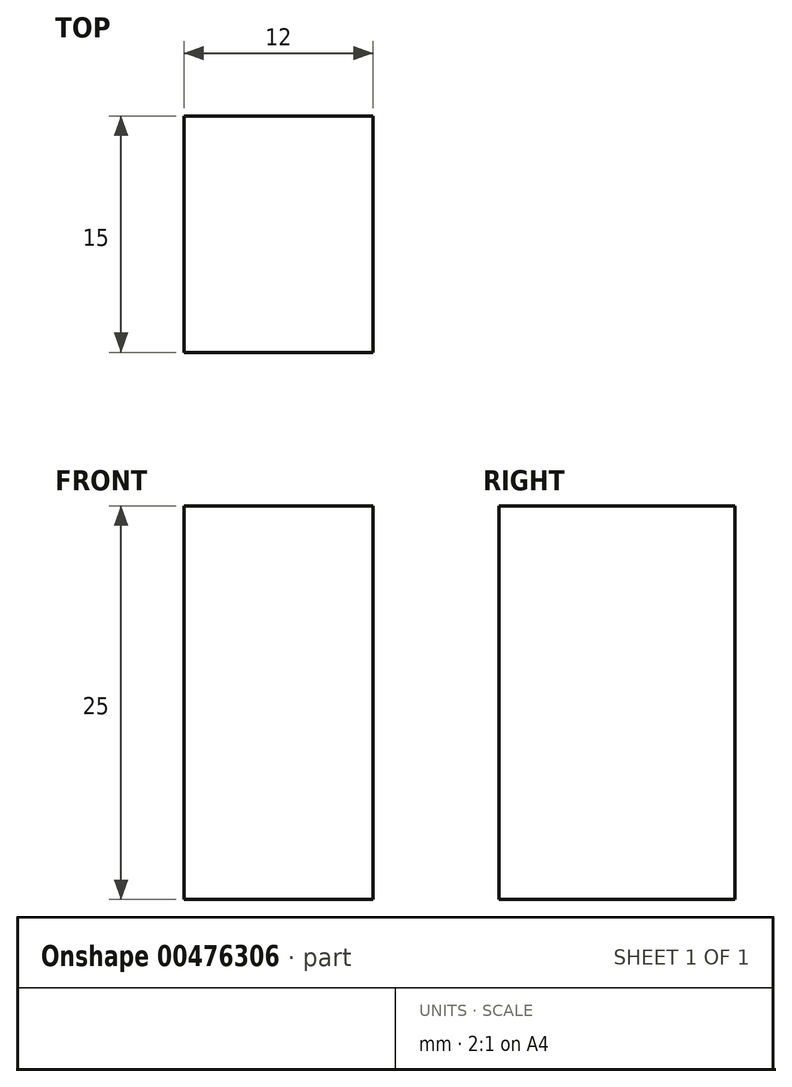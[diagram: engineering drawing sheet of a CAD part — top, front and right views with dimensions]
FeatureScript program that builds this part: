
annotation { "Feature Type Name" : "Feature", "Feature Type Description" : "" }
export const myFeature = defineFeature(function(context is Context, id is Id, definition is map)
    precondition{}
    {
        {
            var Q0;
            Q0=qCreatedBy(makeId("Top.planeOp"),FACE);
            var sketch = newSketch(context, id + "F0", { "sketchPlane" : qUnion([Q0])});
            skLineSegment(sketch, "E0.bottom", {"start": v(0, 0) * mm, "end": v(12, 0) * mm});
            skLineSegment(sketch, "E0.top", {"start": v(0, 15) * mm, "end": v(12, 15) * mm});
            skLineSegment(sketch, "E0.left", {"start": v(0, 0) * mm, "end": v(0, 15) * mm});
            skLineSegment(sketch, "E0.right", {"start": v(12, 0) * mm, "end": v(12, 15) * mm});
            skSolve(sketch);
        }
        {
            var Q0;
            Q0=makeQuery(id+"F0.imprint","IMPRINT",FACE,{"disambiguationData":[TD([[makeQuery(id+"F0.imprint","IMPRINT",EDGE,{"derivedFrom":sQuery(id+"F0.wireOp",EDGE,"E0.bottom")}),1.0]])]});
            extrude(context, id + "F1", {"entities" : qUnion([Q0]), "depth" : 25 * mm});
        }
    });
